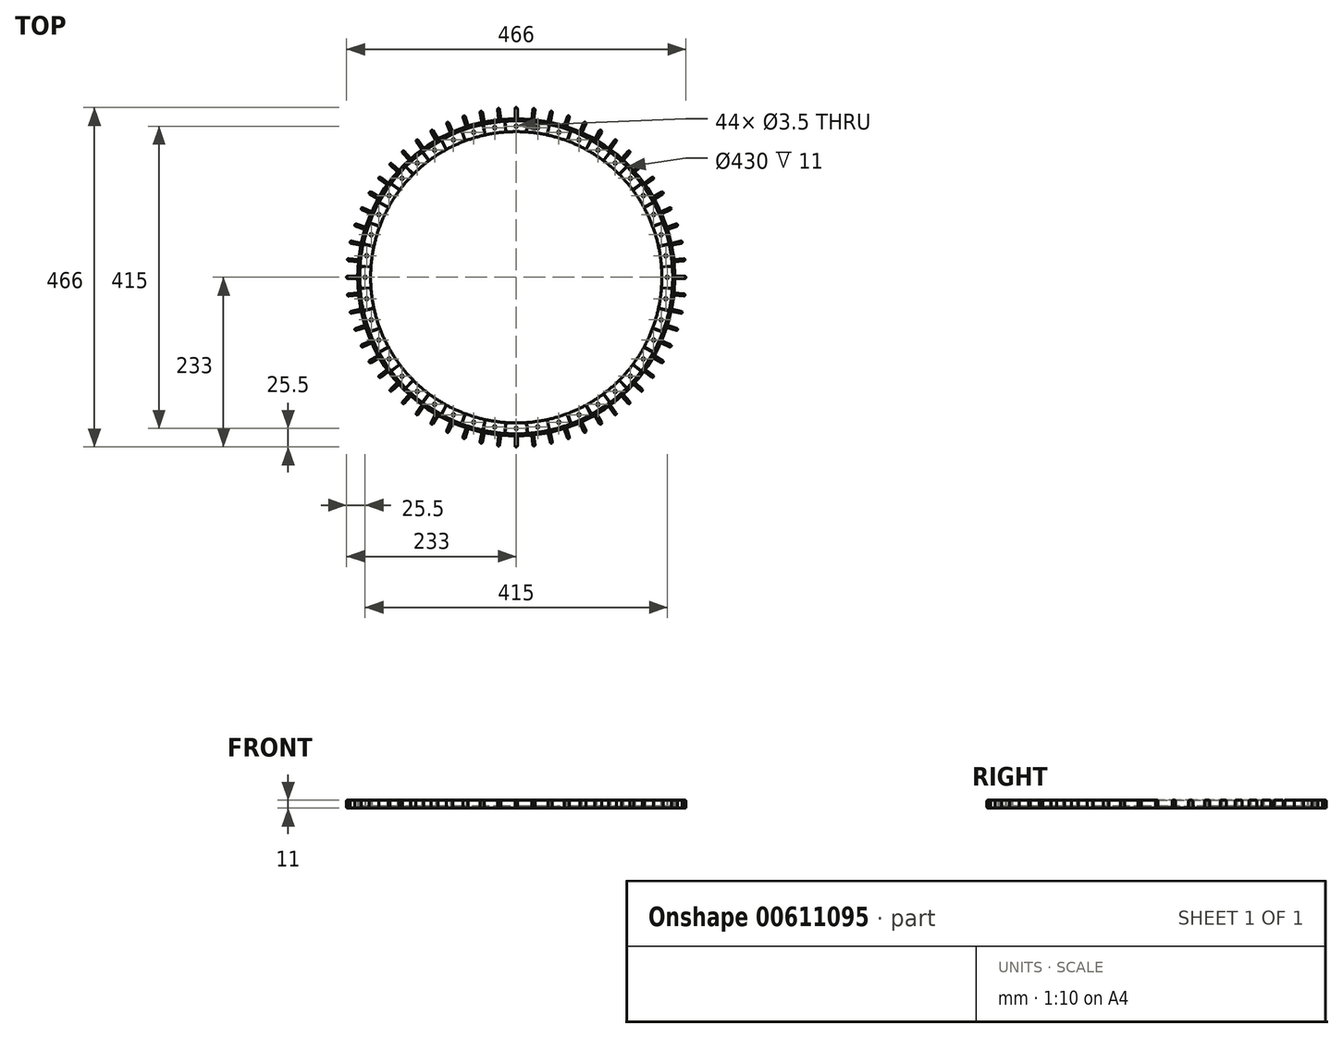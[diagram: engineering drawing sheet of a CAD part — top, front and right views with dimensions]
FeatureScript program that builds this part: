
annotation { "Feature Type Name" : "Feature", "Feature Type Description" : "" }
export const myFeature = defineFeature(function(context is Context, id is Id, definition is map)
    precondition{}
    {
        {
            var Q0;
            Q0=qCreatedBy(makeId("Top.planeOp"),FACE);
            var sketch = newSketch(context, id + "F0", { "sketchPlane" : qUnion([Q0])});
            skCircle(sketch, "E0", {"center": v(0, 0) * mm, "radius": 215 * mm});
            skCircle(sketch, "E1", {"center": v(0, 0) * mm, "radius": 230 * mm});
            skLineSegment(sketch, "E2", {"start": v(0, 0) * mm, "end": v(0, 273.03) * mm});
            skLineSegment(sketch, "E3.bottom", {"start": v(-1.5, 233) * mm, "end": v(1.5, 233) * mm});
            skLineSegment(sketch, "E3.top", {"start": v(-1.5, 218) * mm, "end": v(1.5, 218) * mm});
            skLineSegment(sketch, "E3.left", {"start": v(-1.5, 233) * mm, "end": v(-1.5, 218) * mm});
            skLineSegment(sketch, "E3.right", {"start": v(1.5, 233) * mm, "end": v(1.5, 218) * mm});
            skPoint(sketch, "E3.middle", {"position": v(0, 225.5) * mm});
            skCircle(sketch, "E4", {"center": v(0, 0) * mm, "radius": 200 * mm});
            skCircle(sketch, "E5", {"center": v(0, 0) * mm, "radius": 218 * mm});
            skLineSegment(sketch, "E6.top", {"start": v(-1.5, 217.08) * mm, "end": v(1.5, 217.08) * mm});
            skLineSegment(sketch, "E6.left", {"start": v(-1.5, 218) * mm, "end": v(-1.5, 217.08) * mm});
            skLineSegment(sketch, "E6.right", {"start": v(1.5, 218) * mm, "end": v(1.5, 217.08) * mm});
            skCircle(sketch, "E7", {"center": v(0, 0) * mm, "radius": 233 * mm});
            skLineSegment(sketch, "E8", {"start": v(0, 241.25) * mm, "end": v(-25.84, 241.25) * mm});
            skPoint(sketch, "E9", {"position": v(0, 207.5) * mm});
            skLineSegment(sketch, "E10", {"start": v(0, 0) * mm, "end": v(-18.88, 260.56) * mm});
            skLineSegment(sketch, "E11", {"start": v(0, 0) * mm, "end": v(17.95, 247.64) * mm});
            skPoint(sketch, "E12", {"position": v(-15.54, 214.44) * mm});
            skPoint(sketch, "E13", {"position": v(-14.46, 199.48) * mm});
            skPoint(sketch, "E14", {"position": v(14.46, 199.48) * mm});
            skPoint(sketch, "E15", {"position": v(15.54, 214.44) * mm});
            skPoint(sketch, "E16", {"position": v(0, 215) * mm});
            skPoint(sketch, "E17", {"position": v(0, 200) * mm});
            skSolve(sketch);
        }
        {
            var Q0;
            {var subQ0=sQuery(id+"F0.wireOp",EDGE,"E3.left");var subQ1=sQuery(id+"F0.wireOp",EDGE,"E1");var subQ2=makeQuery(id+"F0.imprint","INTERSECT",VERTEX,{"derivedFrom":[subQ1,subQ0]});Q0=makeQuery(id+"F0.imprint","IMPRINT",FACE,{"disambiguationData":[TD([[makeQuery(id+"F0.imprint","IMPRINT",EDGE,{"disambiguationData":[TD([[subQ2,1.0]])],"derivedFrom":subQ1}),1.0]])]});}
            var Q1;
            {var subQ0=sQuery(id+"F0.wireOp",EDGE,"E3.right");var subQ1=sQuery(id+"F0.wireOp",EDGE,"E1");var subQ2=makeQuery(id+"F0.imprint","INTERSECT",VERTEX,{"derivedFrom":[subQ1,subQ0]});Q1=makeQuery(id+"F0.imprint","IMPRINT",FACE,{"disambiguationData":[TD([[makeQuery(id+"F0.imprint","IMPRINT",EDGE,{"disambiguationData":[TD([[subQ2,-1.0]])],"derivedFrom":subQ1}),1.0]])]});}
            var Q2;
            {var subQ0=sQuery(id+"F0.wireOp",EDGE,"E6.top");var subQ5=sQuery(id+"F0.wireOp",EDGE,"E6.right");var subQ7=makeQuery(id+"F0.imprint","INTERSECT",VERTEX,{"derivedFrom":[subQ0,subQ5]});Q2=makeQuery(id+"F0.imprint","IMPRINT",FACE,{"disambiguationData":[TD([[makeQuery(id+"F0.imprint","IMPRINT",EDGE,{"disambiguationData":[TD([[subQ7,1.0]])],"derivedFrom":subQ0}),1.0]])]});}
            var Q3;
            {var subQ0=sQuery(id+"F0.wireOp",EDGE,"E6.top");var subQ5=sQuery(id+"F0.wireOp",EDGE,"E6.left");var subQ6=makeQuery(id+"F0.imprint","INTERSECT",VERTEX,{"derivedFrom":[subQ0,subQ5]});Q3=makeQuery(id+"F0.imprint","IMPRINT",FACE,{"disambiguationData":[TD([[makeQuery(id+"F0.imprint","IMPRINT",EDGE,{"disambiguationData":[TD([[subQ6,-1.0]])],"derivedFrom":subQ0}),1.0]])]});}
            var Q4;
            {var subQ0=sQuery(id+"F0.wireOp",EDGE,"E3.right");var subQ1=sQuery(id+"F0.wireOp",EDGE,"E1");var subQ2=makeQuery(id+"F0.imprint","INTERSECT",VERTEX,{"derivedFrom":[subQ1,subQ0]});Q4=makeQuery(id+"F0.imprint","IMPRINT",FACE,{"disambiguationData":[TD([[makeQuery(id+"F0.imprint","IMPRINT",EDGE,{"disambiguationData":[TD([[subQ2,-1.0]])],"derivedFrom":subQ1}),-1.0]])]});}
            var Q5;
            {var subQ0=sQuery(id+"F0.wireOp",EDGE,"E3.left");var subQ1=sQuery(id+"F0.wireOp",EDGE,"E1");var subQ2=makeQuery(id+"F0.imprint","INTERSECT",VERTEX,{"derivedFrom":[subQ1,subQ0]});Q5=makeQuery(id+"F0.imprint","IMPRINT",FACE,{"disambiguationData":[TD([[makeQuery(id+"F0.imprint","IMPRINT",EDGE,{"disambiguationData":[TD([[subQ2,1.0]])],"derivedFrom":subQ1}),-1.0]])]});}
            var Q6;
            Q6=makeQuery(id+"F0.imprint","IMPRINT",FACE,{"disambiguationData":[TD([[makeQuery(id+"F0.imprint","IMPRINT",EDGE,{"derivedFrom":sQuery(id+"F0.wireOp",EDGE,"E0")}),-1.0]])]});
            var Q7;
            {var subQ3=sQuery(id+"F0.wireOp",EDGE,"E2");var subQ9=sQuery(id+"F0.wireOp",EDGE,"E0");var subQ10=makeQuery(id+"F0.imprint","INTERSECT",VERTEX,{"derivedFrom":[subQ9,subQ3]});Q7=makeQuery(id+"F0.imprint","IMPRINT",FACE,{"disambiguationData":[TD([[makeQuery(id+"F0.imprint","IMPRINT",EDGE,{"disambiguationData":[TD([[subQ10,1.0]])],"derivedFrom":subQ9}),-1.0]])]});}
            var Q8;
            {var subQ3=sQuery(id+"F0.wireOp",EDGE,"E2");var subQ9=sQuery(id+"F0.wireOp",EDGE,"E0");var subQ10=makeQuery(id+"F0.imprint","INTERSECT",VERTEX,{"derivedFrom":[subQ9,subQ3]});Q8=makeQuery(id+"F0.imprint","IMPRINT",FACE,{"disambiguationData":[TD([[makeQuery(id+"F0.imprint","IMPRINT",EDGE,{"disambiguationData":[TD([[subQ10,-1.0]])],"derivedFrom":subQ9}),-1.0]])]});}
            extrude(context, id + "F1", {"entities" : qUnion([Q0, Q1, Q2, Q3, Q4, Q5, Q6, Q7, Q8]), "depth" : 11 * mm, "offsetDistance" : 25 * mm});
        }
        {
            var Q0;
            {var subQ0=sQuery(id+"F0.wireOp",EDGE,"E6.top");var subQ5=sQuery(id+"F0.wireOp",EDGE,"E6.right");var subQ7=makeQuery(id+"F0.imprint","INTERSECT",VERTEX,{"derivedFrom":[subQ0,subQ5]});Q0=makeQuery(id+"F0.imprint","IMPRINT",FACE,{"disambiguationData":[TD([[makeQuery(id+"F0.imprint","IMPRINT",EDGE,{"disambiguationData":[TD([[subQ7,1.0]])],"derivedFrom":subQ0}),1.0]])]});}
            var Q1;
            {var subQ0=sQuery(id+"F0.wireOp",EDGE,"E6.top");var subQ5=sQuery(id+"F0.wireOp",EDGE,"E6.left");var subQ6=makeQuery(id+"F0.imprint","INTERSECT",VERTEX,{"derivedFrom":[subQ0,subQ5]});Q1=makeQuery(id+"F0.imprint","IMPRINT",FACE,{"disambiguationData":[TD([[makeQuery(id+"F0.imprint","IMPRINT",EDGE,{"disambiguationData":[TD([[subQ6,-1.0]])],"derivedFrom":subQ0}),1.0]])]});}
            extrude(context, id + "F2", {"entities" : qUnion([Q0, Q1]), "depth" : 11 * mm, "offsetDistance" : 25 * mm});
        }
        {
            var Q0;
            Q0=qCreatedBy(makeId("Right.planeOp"),FACE);
            var sketch = newSketch(context, id + "F3", { "sketchPlane" : qUnion([Q0])});
            skLineSegment(sketch, "E18", {"start": v(0, -68.59) * mm, "end": v(0, 58.45) * mm});
            skSolve(sketch);
        }
        {
            var Q0;
            Q0=makeQuery(id+"F1.opExtrude","CAP_EDGE",EDGE,{"disambiguationData":[OSD([sQuery(id+"F0.wireOp",EDGE,"E3.right")])],"isStart":false});
            var Q1;
            Q1=makeQuery(id+"F1.opExtrude","CAP_EDGE",EDGE,{"disambiguationData":[OSD([sQuery(id+"F0.wireOp",EDGE,"E3.left")])],"isStart":false});
            var Q2;
            Q2=makeQuery(id+"F1.opExtrude","CAP_EDGE",EDGE,{"disambiguationData":[OSD([sQuery(id+"F0.wireOp",EDGE,"E3.left")])],"isStart":true});
            var Q3;
            Q3=makeQuery(id+"F1.opExtrude","CAP_EDGE",EDGE,{"disambiguationData":[OSD([sQuery(id+"F0.wireOp",EDGE,"E3.right")])],"isStart":true});
            var Q4;
            Q4=makeQuery(id+"F1.opExtrude","SWEPT_EDGE",EDGE,{"disambiguationData":[OSD([sQuery(id+"F0.wireOp",EDGE,"E3.left"),sQuery(id+"F0.wireOp",EDGE,"E7")])]});
            var Q5;
            Q5=makeQuery(id+"F1.opExtrude","SWEPT_EDGE",EDGE,{"disambiguationData":[OSD([sQuery(id+"F0.wireOp",EDGE,"E3.right"),sQuery(id+"F0.wireOp",EDGE,"E7")])]});
            var Q6;
            Q6=makeQuery(id+"F1.opExtrude","CAP_EDGE",EDGE,{"disambiguationData":[OSD([sQuery(id+"F0.wireOp",EDGE,"E7")])],"isStart":true});
            var Q7;
            Q7=makeQuery(id+"F1.opExtrude","CAP_EDGE",EDGE,{"disambiguationData":[OSD([sQuery(id+"F0.wireOp",EDGE,"E7")])],"isStart":false});
            fillet(context, id + "F4", {"entities" : qUnion([Q0, Q1, Q2, Q3, Q4, Q5, Q6, Q7]), "radius" : 1.5 * mm, "tangentPropagation" : true, "allowEdgeOverflow" : false});
        }
        {
            var Q0;
            Q0=makeQuery(id+"F1.opExtrude","SWEPT_BODY",BODY,{"disambiguationData":[OSD([sQuery(id+"F0.wireOp",EDGE,"E3.left"),sQuery(id+"F0.wireOp",EDGE,"E3.right"),sQuery(id+"F0.wireOp",EDGE,"E3.top"),sQuery(id+"F0.wireOp",EDGE,"E7")])]});
            var Q1;
            Q1=sQuery(id+"F3.wireOp",EDGE,"E18");
            circularPattern(context, id + "F5", {"entities" : qUnion([Q0]), "axis" : qUnion([Q1]), "angle" : 360 * degree, "instanceCount" : 60, "equalSpace" : true});
        }
        {
            var Q0;
            {var subQ0=sQuery(id+"F0.wireOp",EDGE,"E2");var subQ1=sQuery(id+"F0.wireOp",EDGE,"E0");var subQ2=makeQuery(id+"F0.imprint","INTERSECT",VERTEX,{"derivedFrom":[subQ1,subQ0]});Q0=makeQuery(id+"F0.imprint","IMPRINT",FACE,{"disambiguationData":[TD([[makeQuery(id+"F0.imprint","IMPRINT",EDGE,{"disambiguationData":[TD([[subQ2,-1.0]])],"derivedFrom":subQ1}),1.0]])]});}
            var Q1;
            {var subQ0=sQuery(id+"F0.wireOp",EDGE,"E2");var subQ1=sQuery(id+"F0.wireOp",EDGE,"E0");var subQ2=makeQuery(id+"F0.imprint","INTERSECT",VERTEX,{"derivedFrom":[subQ1,subQ0]});Q1=makeQuery(id+"F0.imprint","IMPRINT",FACE,{"disambiguationData":[TD([[makeQuery(id+"F0.imprint","IMPRINT",EDGE,{"disambiguationData":[TD([[subQ2,1.0]])],"derivedFrom":subQ1}),1.0]])]});}
            extrude(context, id + "F6", {"entities" : qUnion([Q0, Q1]), "depth" : 3 * mm, "offsetDistance" : 25 * mm});
        }
        {
            var Q0;
            Q0=sQuery(id+"F0.wireOp",VERTEX,"E9");
            var Q1;
            Q1=makeQuery(id+"F6.opExtrude","SWEPT_BODY",BODY,{"disambiguationData":[OSD([sQuery(id+"F0.wireOp",EDGE,"E0"),sQuery(id+"F0.wireOp",EDGE,"E4"),sQuery(id+"F0.wireOp",EDGE,"E10"),sQuery(id+"F0.wireOp",EDGE,"E11")])]});
            hole(context, id + "F7", {"style" : HoleStyle.C_SINK, "endStyle" : HoleEndStyle.THROUGH, "oppositeDirection" : true, "holeDiameter" : 3.5 * mm, "cSinkDiameter" : 5 * mm, "cSinkAngle" : 90 * degree, "majorDiameter" : 5 * mm, "isTappedThrough" : true, "tappedDepth" : 12 * mm, "tapClearance" : 3, "locations" : qUnion([Q0]), "scope" : qUnion([Q1])});
        }
        {
            var Q0;
            Q0=makeQuery(id+"F6.opExtrude","SWEPT_BODY",BODY,{"disambiguationData":[OSD([sQuery(id+"F0.wireOp",EDGE,"E0"),sQuery(id+"F0.wireOp",EDGE,"E4"),sQuery(id+"F0.wireOp",EDGE,"E10"),sQuery(id+"F0.wireOp",EDGE,"E11")])]});
            var Q1;
            Q1=sQuery(id+"F3.wireOp",EDGE,"E18");
            circularPattern(context, id + "F8", {"entities" : qUnion([Q0]), "axis" : qUnion([Q1]), "angle" : 360 * degree, "instanceCount" : 44, "equalSpace" : true});
        }
    });
